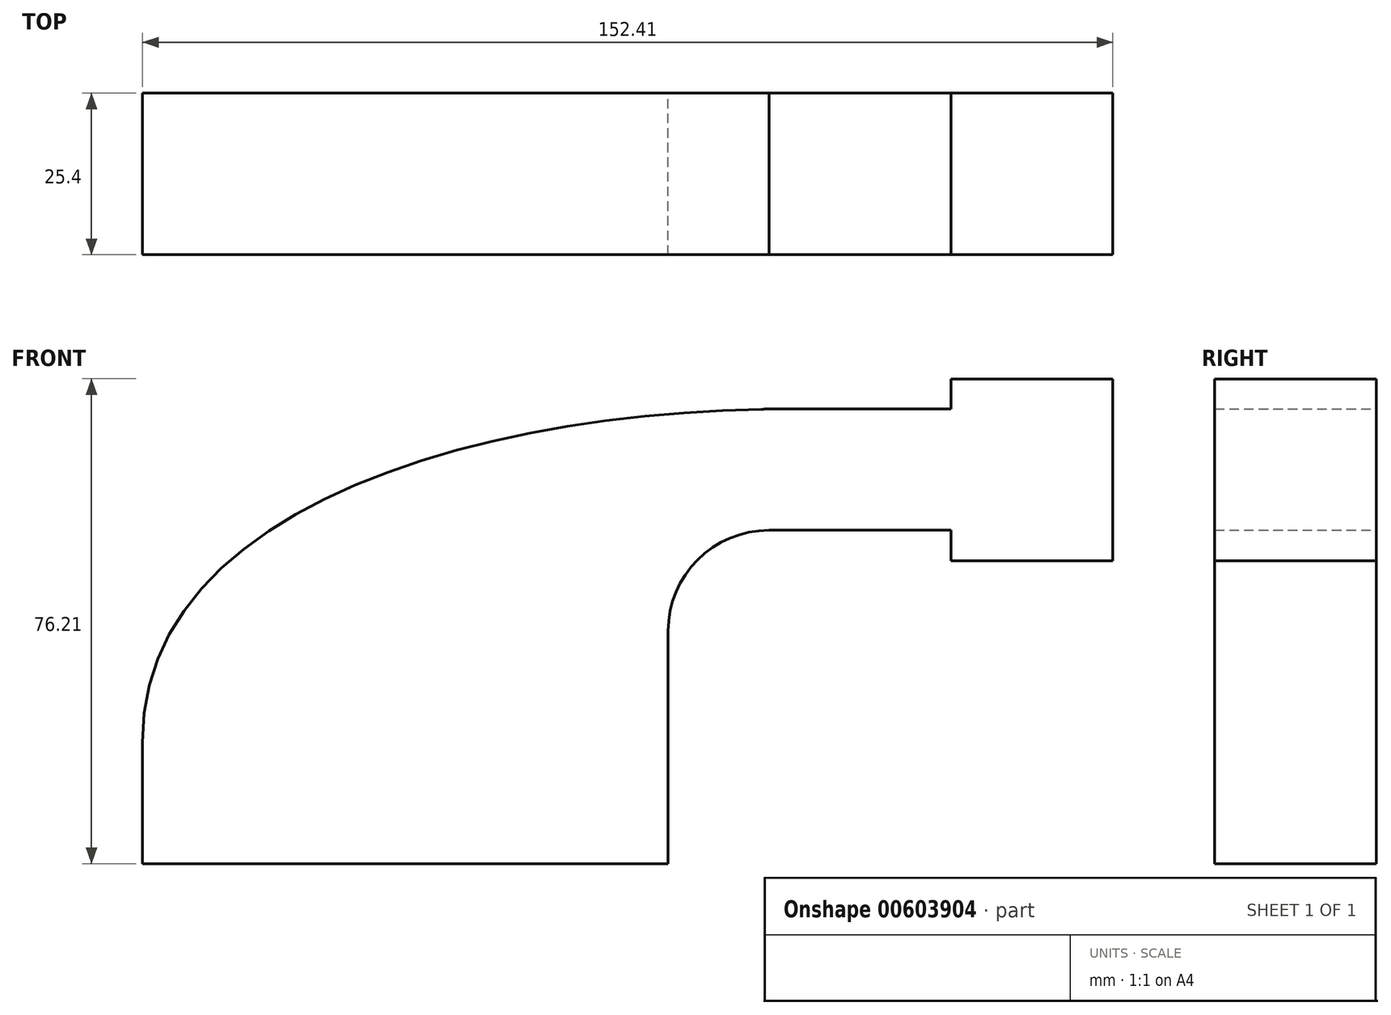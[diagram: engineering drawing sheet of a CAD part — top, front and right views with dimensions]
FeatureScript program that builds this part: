
annotation { "Feature Type Name" : "Feature", "Feature Type Description" : "" }
export const myFeature = defineFeature(function(context is Context, id is Id, definition is map)
    precondition{}
    {
        {
            var Q0;
            Q0=qCreatedBy(makeId("Front.planeOp"),FACE);
            var sketch = newSketch(context, id + "F0", { "sketchPlane" : qUnion([Q0])});
            skLineSegment(sketch, "E0.bottom", {"start": v(41.28, -9.52) * mm, "end": v(-41.27, -9.53) * mm});
            skLineSegment(sketch, "E0.top", {"start": v(41.27, 9.53) * mm, "end": v(-41.28, 9.53) * mm});
            skLineSegment(sketch, "E0.left", {"start": v(41.28, -9.52) * mm, "end": v(41.28, 9.53) * mm});
            skLineSegment(sketch, "E0.right", {"start": v(-41.27, -9.53) * mm, "end": v(-41.28, 9.53) * mm});
            skPoint(sketch, "E0.middle", {"position": v(0, 0) * mm});
            skLineSegment(sketch, "E1.bottom", {"start": v(60.32, 38.1) * mm, "end": v(111.12, 38.1) * mm});
            skLineSegment(sketch, "E1.top", {"start": v(60.33, 66.68) * mm, "end": v(111.12, 66.68) * mm});
            skLineSegment(sketch, "E1.left", {"start": v(60.32, 38.1) * mm, "end": v(60.32, 66.68) * mm});
            skLineSegment(sketch, "E1.right", {"start": v(111.12, 38.1) * mm, "end": v(111.12, 66.68) * mm});
            skPoint(sketch, "E1.middle", {"position": v(85.72, 52.39) * mm});
            skLineSegment(sketch, "E2", {"start": v(41.27, 9.53) * mm, "end": v(41.27, 27) * mm});
            skArc(sketch, "E3", {"start": v(41.27, 27) * mm, "mid": v(45.92, 38.23) * mm, "end": v(57.15, 42.88) * mm});
            skLineSegment(sketch, "E4", {"start": v(57.15, 42.88) * mm, "end": v(106.4, 42.88) * mm});
            skLineSegment(sketch, "E5.0", {"start": v(57.15, 61.93) * mm, "end": v(106.4, 61.93) * mm});
            skArc(sketch, "E5.1", {"start": v(22.23, 27) * mm, "mid": v(32.45, 51.7) * mm, "end": v(57.15, 61.93) * mm});
            skLineSegment(sketch, "E5.2", {"start": v(22.23, 9.53) * mm, "end": v(22.23, 27) * mm});
            skLineSegment(sketch, "E6", {"start": v(85.72, 38.1) * mm, "end": v(85.72, 66.68) * mm});
            skFitSpline(sketch, "E7", {"points": [v(-41.28, 9.52) * mm, v(57.15, 61.93) * mm], "startDerivative": vector(-0.85, 109.31) * mm, "endDerivative": vector(141.05, 2.07) * mm});
            skSolve(sketch);
        }
        {
            var Q0;
            Q0=makeQuery(id+"F0.imprint","IMPRINT",FACE,{"disambiguationData":[TD([[makeQuery(id+"F0.imprint","IMPRINT",EDGE,{"derivedFrom":sQuery(id+"F0.wireOp",EDGE,"E0.bottom")}),-1.0]])]});
            var Q1;
            {var subQ3=sQuery(id+"F0.wireOp",EDGE,"E5.2");Q1=makeQuery(id+"F0.imprint","IMPRINT",FACE,{"disambiguationData":[TD([[makeQuery(id+"F0.imprint","IMPRINT",EDGE,{"derivedFrom":subQ3}),1.0]])]});}
            var Q2;
            {var subQ4=sQuery(id+"F0.wireOp",EDGE,"E1.right");Q2=makeQuery(id+"F0.imprint","IMPRINT",FACE,{"disambiguationData":[TD([[makeQuery(id+"F0.imprint","IMPRINT",EDGE,{"derivedFrom":subQ4}),1.0]])]});}
            var Q3;
            {var subQ1=sQuery(id+"F0.wireOp",EDGE,"E2");Q3=makeQuery(id+"F0.imprint","IMPRINT",FACE,{"disambiguationData":[TD([[makeQuery(id+"F0.imprint","IMPRINT",EDGE,{"derivedFrom":subQ1}),1.0]])]});}
            var Q4;
            {var subQ0=sQuery(id+"F0.wireOp",EDGE,"E4");var subQ1=sQuery(id+"F0.wireOp",EDGE,"E1.left");var subQ2=makeQuery(id+"F0.imprint","INTERSECT",VERTEX,{"derivedFrom":[subQ1,subQ0]});Q4=makeQuery(id+"F0.imprint","IMPRINT",FACE,{"disambiguationData":[TD([[makeQuery(id+"F0.imprint","IMPRINT",EDGE,{"disambiguationData":[TD([[subQ2,-1.0]])],"derivedFrom":subQ1}),-1.0]])]});}
            extrude(context, id + "F1", {"entities" : qUnion([Q0, Q1, Q2, Q3, Q4]), "depth" : 25.4 * mm, "offsetDistance" : 25.4 * mm});
        }
    });
